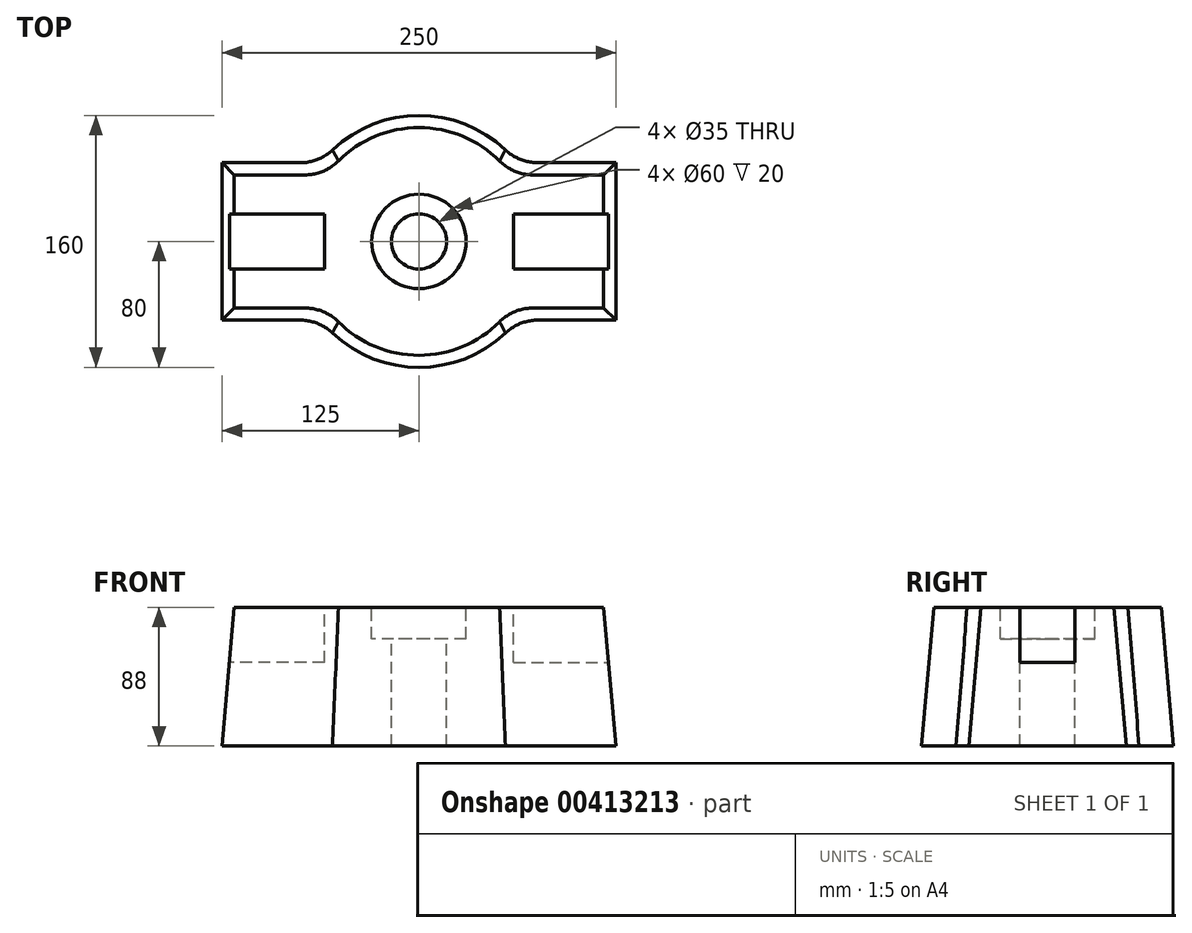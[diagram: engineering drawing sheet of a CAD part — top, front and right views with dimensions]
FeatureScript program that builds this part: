
annotation { "Feature Type Name" : "Feature", "Feature Type Description" : "" }
export const myFeature = defineFeature(function(context is Context, id is Id, definition is map)
    precondition{}
    {
        {
            var Q0;
            Q0=qCreatedBy(makeId("Top.planeOp"),FACE);
            var sketch = newSketch(context, id + "F0", { "sketchPlane" : qUnion([Q0])});
            skCircle(sketch, "E0", {"center": v(0, 0) * mm, "radius": 80 * mm});
            skLineSegment(sketch, "E1.bottom", {"start": v(-125, 50) * mm, "end": v(125, 50) * mm});
            skLineSegment(sketch, "E1.top", {"start": v(-125, -50) * mm, "end": v(125, -50) * mm});
            skLineSegment(sketch, "E1.left", {"start": v(-125, 50) * mm, "end": v(-125, -50) * mm});
            skLineSegment(sketch, "E1.right", {"start": v(125, 50) * mm, "end": v(125, -50) * mm});
            skSolve(sketch);
        }
        {
            var Q0;
            {var subQ0=sQuery(id+"F0.wireOp",EDGE,"E1.bottom");var subQ1=sQuery(id+"F0.wireOp",EDGE,"E0");var subQ2=makeQuery(id+"F0.imprint","INTERSECT",VERTEX,{"disambiguationData":[OD(0.0)],"derivedFrom":[subQ1,subQ0]});Q0=makeQuery(id+"F0.imprint","IMPRINT",FACE,{"disambiguationData":[TD([[makeQuery(id+"F0.imprint","IMPRINT",EDGE,{"disambiguationData":[TD([[subQ2,1.0]])],"derivedFrom":subQ1}),1.0]])]});}
            var Q1;
            {var subQ5=sQuery(id+"F0.wireOp",EDGE,"E1.left");Q1=makeQuery(id+"F0.imprint","IMPRINT",FACE,{"disambiguationData":[TD([[makeQuery(id+"F0.imprint","IMPRINT",EDGE,{"derivedFrom":subQ5}),1.0]])]});}
            var Q2;
            {var subQ0=sQuery(id+"F0.wireOp",EDGE,"E1.top");var subQ1=sQuery(id+"F0.wireOp",EDGE,"E0");var subQ2=makeQuery(id+"F0.imprint","INTERSECT",VERTEX,{"disambiguationData":[OD(0.0)],"derivedFrom":[subQ1,subQ0]});Q2=makeQuery(id+"F0.imprint","IMPRINT",FACE,{"disambiguationData":[TD([[makeQuery(id+"F0.imprint","IMPRINT",EDGE,{"disambiguationData":[TD([[subQ2,-1.0]])],"derivedFrom":subQ1}),1.0]])]});}
            var Q3;
            {var subQ5=sQuery(id+"F0.wireOp",EDGE,"E1.right");Q3=makeQuery(id+"F0.imprint","IMPRINT",FACE,{"disambiguationData":[TD([[makeQuery(id+"F0.imprint","IMPRINT",EDGE,{"derivedFrom":subQ5}),-1.0]])]});}
            var Q4;
            {var subQ0=sQuery(id+"F0.wireOp",EDGE,"E1.bottom");var subQ1=sQuery(id+"F0.wireOp",EDGE,"E0");var subQ2=makeQuery(id+"F0.imprint","INTERSECT",VERTEX,{"disambiguationData":[OD(0.0)],"derivedFrom":[subQ1,subQ0]});Q4=makeQuery(id+"F0.imprint","IMPRINT",FACE,{"disambiguationData":[TD([[makeQuery(id+"F0.imprint","IMPRINT",EDGE,{"disambiguationData":[TD([[subQ2,-1.0]])],"derivedFrom":subQ1}),1.0]])]});}
            extrude(context, id + "F1", {"entities" : qUnion([Q0, Q1, Q2, Q3, Q4]), "depth" : 88 * mm, "hasDraft" : true, "draftAngle" : 5 * degree, "draftPullDirection" : true});
        }
        {
            var Q0;
            Q0=makeQuery(id+"F1.opExtrude","CAP_FACE",FACE,{"disambiguationData":[OSD([sQuery(id+"F0.wireOp",EDGE,"E0"),sQuery(id+"F0.wireOp",EDGE,"E1.bottom"),sQuery(id+"F0.wireOp",EDGE,"E1.top"),sQuery(id+"F0.wireOp",EDGE,"E1.left"),sQuery(id+"F0.wireOp",EDGE,"E1.right")])],"isStart":false});
            var sketch = newSketch(context, id + "F2", { "sketchPlane" : qUnion([Q0])});
            skPoint(sketch, "E2", {"position": v(0, 0) * mm});
            skSolve(sketch);
        }
        {
            var Q0;
            Q0=sQuery(id+"F2.wireOp",VERTEX,"E2");
            var Q1;
            Q1=makeQuery(id+"F1.opExtrude","SWEPT_BODY",BODY,{"disambiguationData":[OSD([sQuery(id+"F0.wireOp",EDGE,"E0"),sQuery(id+"F0.wireOp",EDGE,"E1.bottom"),sQuery(id+"F0.wireOp",EDGE,"E1.top"),sQuery(id+"F0.wireOp",EDGE,"E1.left"),sQuery(id+"F0.wireOp",EDGE,"E1.right")])]});
            hole(context, id + "F3", {"style" : HoleStyle.C_BORE, "endStyle" : HoleEndStyle.THROUGH, "holeDiameter" : 35 * mm, "cBoreDiameter" : 60 * mm, "cBoreDepth" : 20 * mm, "isTappedThrough" : true, "tappedDepth" : 12 * mm, "tapClearance" : 3, "locations" : qUnion([Q0]), "scope" : qUnion([Q1])});
        }
        {
            var Q0;
            Q0=makeQuery(id+"F1.opExtrude","CAP_FACE",FACE,{"disambiguationData":[OSD([sQuery(id+"F0.wireOp",EDGE,"E0"),sQuery(id+"F0.wireOp",EDGE,"E1.bottom"),sQuery(id+"F0.wireOp",EDGE,"E1.top"),sQuery(id+"F0.wireOp",EDGE,"E1.left"),sQuery(id+"F0.wireOp",EDGE,"E1.right")])],"isStart":false});
            var sketch = newSketch(context, id + "F4", { "sketchPlane" : qUnion([Q0])});
            skLineSegment(sketch, "E3.bottom", {"start": v(-60, 17.5) * mm, "end": v(-125, 17.5) * mm});
            skLineSegment(sketch, "E3.top", {"start": v(-60, -17.5) * mm, "end": v(-125, -17.5) * mm});
            skLineSegment(sketch, "E3.left", {"start": v(-60, 17.5) * mm, "end": v(-60, -17.5) * mm});
            skLineSegment(sketch, "E3.right", {"start": v(-125, 17.5) * mm, "end": v(-125, -17.5) * mm});
            skLineSegment(sketch, "E4", {"start": v(0, 0) * mm, "end": v(0, 91.65) * mm, "construction": true});
            skPoint(sketch, "E4.endSnap0", {"position": v(0, 72.3) * mm});
            skLineSegment(sketch, "E5.MirrorCS", {"start": v(60, 17.5) * mm, "end": v(125, 17.5) * mm});
            skLineSegment(sketch, "E6.MirrorCS", {"start": v(60, -17.5) * mm, "end": v(125, -17.5) * mm});
            skLineSegment(sketch, "E7.MirrorCS", {"start": v(60, 17.5) * mm, "end": v(60, -17.5) * mm});
            skLineSegment(sketch, "E8.MirrorCS", {"start": v(125, 17.5) * mm, "end": v(125, -17.5) * mm});
            skSolve(sketch);
        }
        {
            var Q0;
            {var subQ0=sQuery(id+"F4.wireOp",EDGE,"E3.left");Q0=makeQuery(id+"F4.imprint","IMPRINT",FACE,{"disambiguationData":[TD([[makeQuery(id+"F4.imprint","IMPRINT",EDGE,{"derivedFrom":subQ0}),-1.0]])]});}
            var Q1;
            {var subQ0=sQuery(id+"F4.wireOp",EDGE,"E7.MirrorCS");Q1=makeQuery(id+"F4.imprint","IMPRINT",FACE,{"disambiguationData":[TD([[makeQuery(id+"F4.imprint","IMPRINT",EDGE,{"derivedFrom":subQ0}),1.0]])]});}
            var Q2;
            {var subQ0=sQuery(id+"F4.wireOp",EDGE,"E3.right");Q2=makeQuery(id+"F4.imprint","IMPRINT",FACE,{"disambiguationData":[TD([[makeQuery(id+"F4.imprint","IMPRINT",EDGE,{"derivedFrom":subQ0}),1.0]])]});}
            var Q3;
            {var subQ0=sQuery(id+"F4.wireOp",EDGE,"E8.MirrorCS");Q3=makeQuery(id+"F4.imprint","IMPRINT",FACE,{"disambiguationData":[TD([[makeQuery(id+"F4.imprint","IMPRINT",EDGE,{"derivedFrom":subQ0}),-1.0]])]});}
            extrude(context, id + "F5", {"entities" : qUnion([Q0, Q1, Q2, Q3]), "operationType" : NewBodyOperationType.REMOVE, "oppositeDirection" : true, "depth" : 35 * mm});
        }
        {
            var Q0;
            {var subQ0=sQuery(id+"F0.wireOp",EDGE,"E1.top");var subQ1=sQuery(id+"F0.wireOp",EDGE,"E0");Q0=makeQuery(id+"F1.opExtrude","SWEPT_EDGE",EDGE,{"disambiguationData":[OSD([subQ1,subQ0]),TDD([makeQuery(id+"F0.imprint","INTERSECT",VERTEX,{"disambiguationData":[OD(1.0)],"derivedFrom":[subQ1,subQ0]})])]});}
            var Q1;
            {var subQ0=sQuery(id+"F0.wireOp",EDGE,"E1.top");var subQ1=sQuery(id+"F0.wireOp",EDGE,"E0");Q1=makeQuery(id+"F1.opExtrude","SWEPT_EDGE",EDGE,{"disambiguationData":[OSD([subQ1,subQ0]),TDD([makeQuery(id+"F0.imprint","INTERSECT",VERTEX,{"disambiguationData":[OD(0.0)],"derivedFrom":[subQ1,subQ0]})])]});}
            var Q2;
            {var subQ0=sQuery(id+"F0.wireOp",EDGE,"E1.bottom");var subQ1=sQuery(id+"F0.wireOp",EDGE,"E0");Q2=makeQuery(id+"F1.opExtrude","SWEPT_EDGE",EDGE,{"disambiguationData":[OSD([subQ1,subQ0]),TDD([makeQuery(id+"F0.imprint","INTERSECT",VERTEX,{"disambiguationData":[OD(1.0)],"derivedFrom":[subQ1,subQ0]})])]});}
            var Q3;
            {var subQ0=sQuery(id+"F0.wireOp",EDGE,"E1.bottom");var subQ1=sQuery(id+"F0.wireOp",EDGE,"E0");Q3=makeQuery(id+"F1.opExtrude","SWEPT_EDGE",EDGE,{"disambiguationData":[OSD([subQ1,subQ0]),TDD([makeQuery(id+"F0.imprint","INTERSECT",VERTEX,{"disambiguationData":[OD(0.0)],"derivedFrom":[subQ1,subQ0]})])]});}
            fillet(context, id + "F6", {"entities" : qUnion([Q0, Q1, Q2, Q3]), "radius" : 30 * mm, "tangentPropagation" : true, "allowEdgeOverflow" : false});
        }
    });
